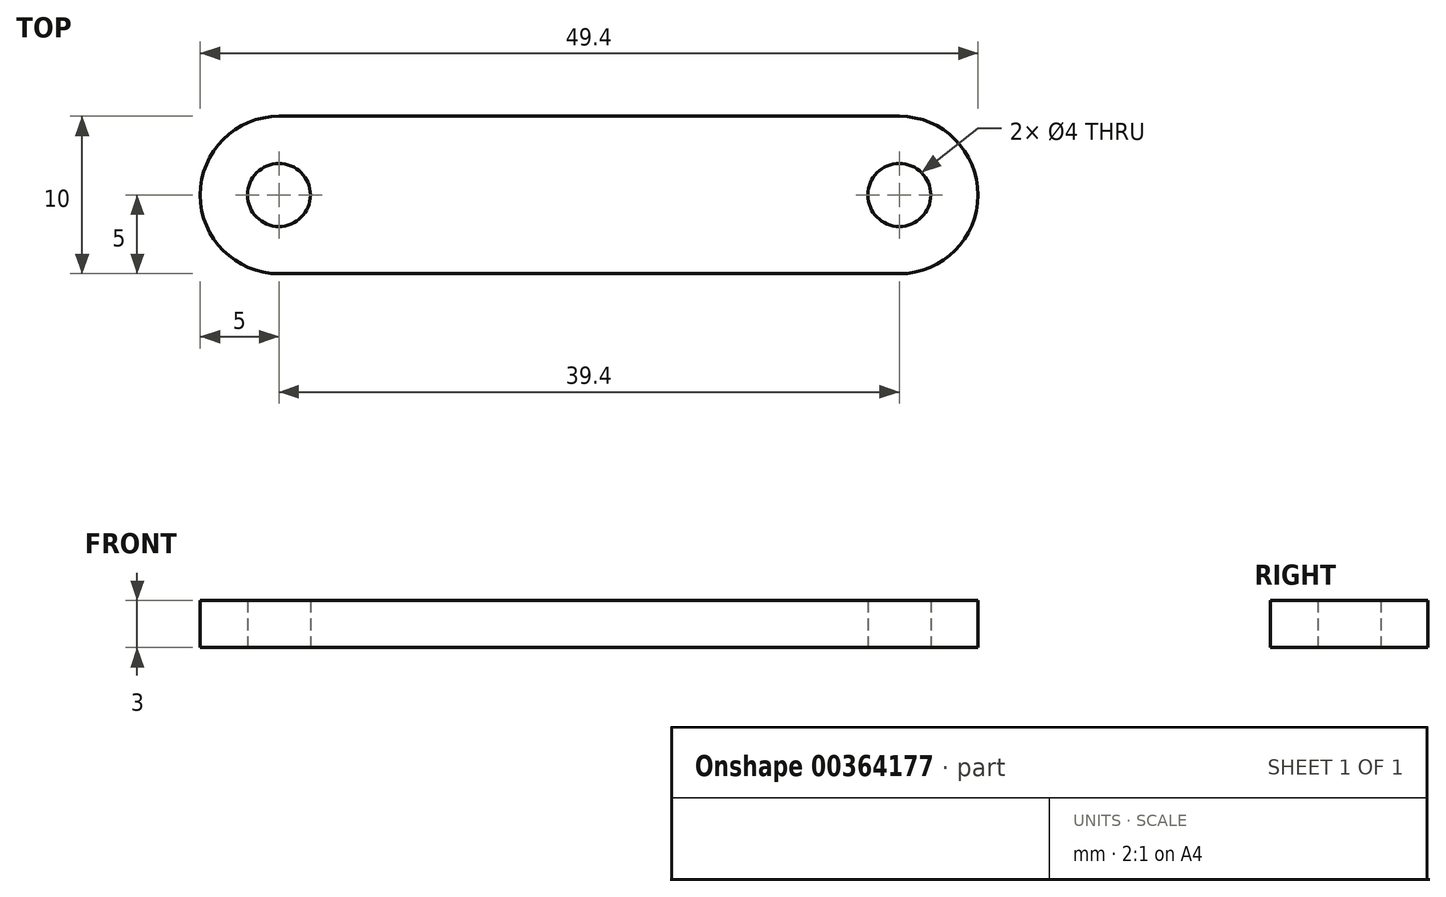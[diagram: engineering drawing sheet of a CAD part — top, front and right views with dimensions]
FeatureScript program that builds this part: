
annotation { "Feature Type Name" : "Feature", "Feature Type Description" : "" }
export const myFeature = defineFeature(function(context is Context, id is Id, definition is map)
    precondition{}
    {
        {
            var Q0;
            Q0=qCreatedBy(makeId("Top.planeOp"),FACE);
            var sketch = newSketch(context, id + "F0", { "sketchPlane" : qUnion([Q0])});
            skLineSegment(sketch, "E0.bottom", {"start": v(19.7, 5) * mm, "end": v(-19.7, 5) * mm});
            skLineSegment(sketch, "E0.top", {"start": v(19.7, -5) * mm, "end": v(-19.7, -5) * mm});
            skPoint(sketch, "E0.middle", {"position": v(0, 0) * mm});
            skCircle(sketch, "E1", {"center": v(-19.7, 0) * mm, "radius": 2 * mm});
            skCircle(sketch, "E2", {"center": v(19.7, 0) * mm, "radius": 2 * mm});
            skArc(sketch, "E3", {"start": v(-19.7, 5) * mm, "mid": v(-24.7, 0) * mm, "end": v(-19.7, -5) * mm});
            skArc(sketch, "E4", {"start": v(19.7, -5) * mm, "mid": v(24.7, 0) * mm, "end": v(19.7, 5) * mm});
            skSolve(sketch);
        }
        {
            var Q0;
            Q0=qSketchRegion(id+"F0",true);
            extrude(context, id + "F1", {"entities" : qUnion([Q0]), "depth" : 3 * mm});
        }
    });
